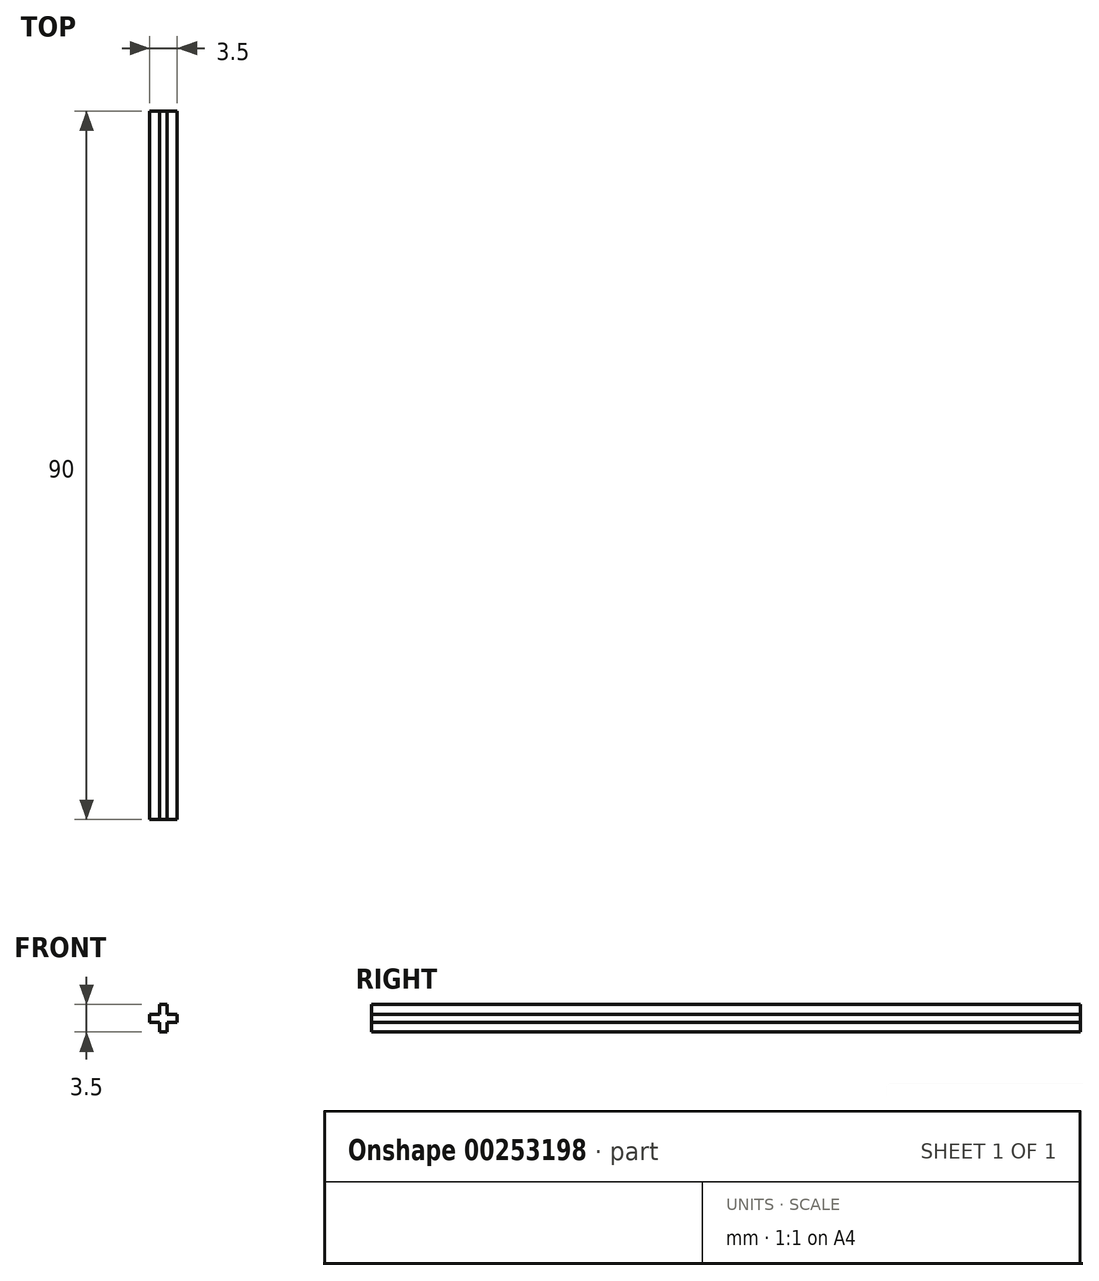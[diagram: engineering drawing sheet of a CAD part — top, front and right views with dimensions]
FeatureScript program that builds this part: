
annotation { "Feature Type Name" : "Feature", "Feature Type Description" : "" }
export const myFeature = defineFeature(function(context is Context, id is Id, definition is map)
    precondition{}
    {
        {
            var Q0;
            Q0=qCreatedBy(makeId("Front.planeOp"),FACE);
            var sketch = newSketch(context, id + "F0", { "sketchPlane" : qUnion([Q0])});
            skLineSegment(sketch, "E0.0", {"start": v(-0.5, 0.5) * mm, "end": v(-0.5, 1.75) * mm});
            skLineSegment(sketch, "E0.1", {"start": v(-0.5, 1.75) * mm, "end": v(0.5, 1.75) * mm});
            skLineSegment(sketch, "E0.2", {"start": v(0.5, 1.75) * mm, "end": v(0.5, 0.5) * mm});
            skLineSegment(sketch, "E0.3", {"start": v(0.5, 0.5) * mm, "end": v(1.75, 0.5) * mm});
            skLineSegment(sketch, "E0.4", {"start": v(1.75, 0.5) * mm, "end": v(1.75, -0.5) * mm});
            skLineSegment(sketch, "E0.5", {"start": v(1.75, -0.5) * mm, "end": v(0.5, -0.5) * mm});
            skLineSegment(sketch, "E0.6", {"start": v(0.5, -0.5) * mm, "end": v(0.5, -1.75) * mm});
            skLineSegment(sketch, "E0.7", {"start": v(0.5, -1.75) * mm, "end": v(-0.5, -1.75) * mm});
            skLineSegment(sketch, "E0.8", {"start": v(-0.5, -1.75) * mm, "end": v(-0.5, -0.5) * mm});
            skLineSegment(sketch, "E0.9", {"start": v(-0.5, -0.5) * mm, "end": v(-1.75, -0.5) * mm});
            skLineSegment(sketch, "E0.10", {"start": v(-1.75, -0.5) * mm, "end": v(-1.75, 0.5) * mm});
            skLineSegment(sketch, "E0.11", {"start": v(-1.75, 0.5) * mm, "end": v(-0.5, 0.5) * mm});
            skLineSegment(sketch, "E1", {"start": v(-0.5, 0.5) * mm, "end": v(0.5, -0.5) * mm, "construction": true});
            skLineSegment(sketch, "E2", {"start": v(0.5, 0.5) * mm, "end": v(-0.5, -0.5) * mm, "construction": true});
            skSolve(sketch);
        }
        {
            var Q0;
            Q0 = qSketchRegion(id + "F0", true);
            extrude(context, id + "F1", {"entities" : qUnion([Q0]), "depth" : 90 * mm});
        }
    });
